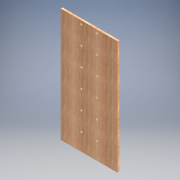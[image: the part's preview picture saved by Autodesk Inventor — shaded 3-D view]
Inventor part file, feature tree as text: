
AUTODESK INVENTOR PART (.ipt)
format: ipt  version: 2021 (Build 250183000, 183)  size: 276,480 bytes
history: native  units: mm
features: sketch x4, extrude x3, other x3, reference x2, projected_geometry x2, hole x1, mirror x1, pattern_linear x1
ambient origin geometry x8: Origin, YZ Plane, XZ Plane, XY Plane, X Axis, Y Axis, Z Axis, Center Point
bodies: Solid1 (feature_tree)
feature tree (17):
  extrude  "Extrusion1"  Depth=1220.0mm
  extrude  "Extrusion2"  TaperAngle=0.0deg  [1 undecoded]
  hole  "Hole1"  [1 undecoded]
  mirror  "Mirror1"
  pattern_linear  "Rectangular Pattern1"  [2 undecoded]
  extrude  "Extrusion3"  [1 undecoded]
  sketch  "Sketch1"  dims[d0=610.0mm d1=1220.0mm]
  sketch  "Sketch2"  dims[d2=20.0mm d3=0.0mm d4=0.0mm d5=0.0mm]
  reference  "Reference1"
  reference  "Reference2"
  sketch  "Sketch3"  dims[d6=8.0mm d7=20.0mm d8=25.0mm d9=2.0mm d10=90.0deg d11=27.3mm d12=20.594885mm d13=60.0mm d15=200.0mm]
  sketch  "Sketch4"  dims[d16=0.0mm d17=0.0mm]
  projected_geometry  "Projected Loop1"
  projected_geometry  "Projected Loop2"
  other  "IMS-00-000.iam"
  other  "IMS-10-000:1"
  other  "IMS-10-001:1"
note: 5 required parameter values undecoded (feature->parameter linkage not recoverable at this tier; creation-order binding heuristic only, values carry confidence <= 0.55)
